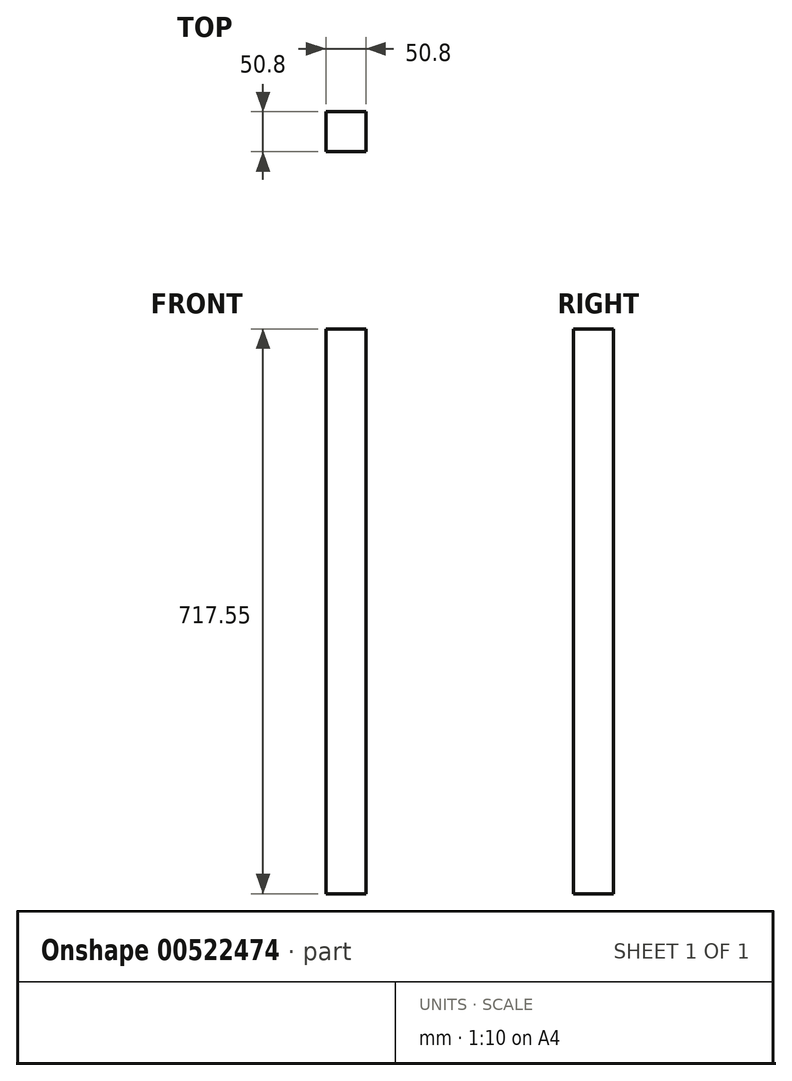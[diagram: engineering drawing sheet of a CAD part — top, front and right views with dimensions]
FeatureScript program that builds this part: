
annotation { "Feature Type Name" : "Feature", "Feature Type Description" : "" }
export const myFeature = defineFeature(function(context is Context, id is Id, definition is map)
    precondition{}
    {
        {
            var Q0;
            Q0=qCreatedBy(makeId("Top.planeOp"),FACE);
            var sketch = newSketch(context, id + "F0", { "sketchPlane" : qUnion([Q0])});
            skLineSegment(sketch, "E0.bottom", {"start": v(-37.03, 17.47) * mm, "end": v(13.77, 17.47) * mm});
            skLineSegment(sketch, "E0.top", {"start": v(-37.03, -33.33) * mm, "end": v(13.77, -33.33) * mm});
            skLineSegment(sketch, "E0.left", {"start": v(-37.03, 17.47) * mm, "end": v(-37.03, -33.33) * mm});
            skLineSegment(sketch, "E0.right", {"start": v(13.77, 17.47) * mm, "end": v(13.77, -33.33) * mm});
            skSolve(sketch);
        }
        {
            var Q0;
            Q0=makeQuery(id+"F0.imprint","IMPRINT",FACE,{"disambiguationData":[TD([[makeQuery(id+"F0.imprint","IMPRINT",EDGE,{"derivedFrom":sQuery(id+"F0.wireOp",EDGE,"E0.bottom")}),-1.0]])]});
            extrude(context, id + "F1", {"entities" : qUnion([Q0]), "depth" : 717.55 * mm, "offsetDistance" : 25.4 * mm});
        }
    });
